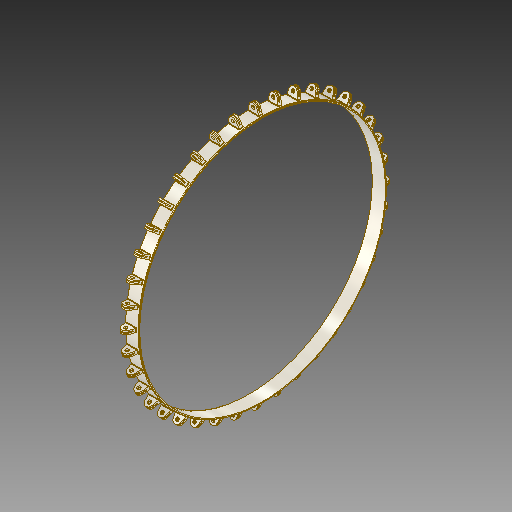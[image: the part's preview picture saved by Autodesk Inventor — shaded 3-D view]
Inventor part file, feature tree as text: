
AUTODESK INVENTOR PART (.ipt)
format: ipt  version: 2019 (Build 230136000, 136)  size: 1,297,408 bytes
history: native  units: mm
features: extrude x3, plane x2, sketch x2, fillet x1, pattern_circular x1
ambient origin geometry x8: Origin, YZ Plane, XZ Plane, XY Plane, X Axis, Y Axis, Z Axis, Center Point
bodies: Body1 (feature_tree)
feature tree (9):
  extrude  "Extrusion1"  Depth=283.0mm
  fillet  "Fillet1"  [1 undecoded]
  extrude  "Extrusion2"  Depth=1.0mm
  plane  "Work Plane7"
  plane  "Work Plane8"
  extrude  "Extrusion3"  Depth=4.0mm
  pattern_circular  "Circular Pattern1"  [2 undecoded]
  sketch  "Sketch2"  dims[d8=280.0mm d9=283.0mm d10=0.0mm]
  sketch  "Sketch9"  dims[d11=15.0mm d12=0.0mm d13=0.5mm d14=4.0mm d53=4.5mm d59=4.0mm d60=0.0mm d62=400.0mm d63=360.0deg d67=8.5mm d68=7.5mm d69=0.5mm d87=0.0mm d89=10.4mm d90=2.0mm d91=2.0mm d92=5.0mm d93=1.0mm d94=0.0mm]
note: 3 required parameter values undecoded (feature->parameter linkage not recoverable at this tier; creation-order binding heuristic only, values carry confidence <= 0.55)
